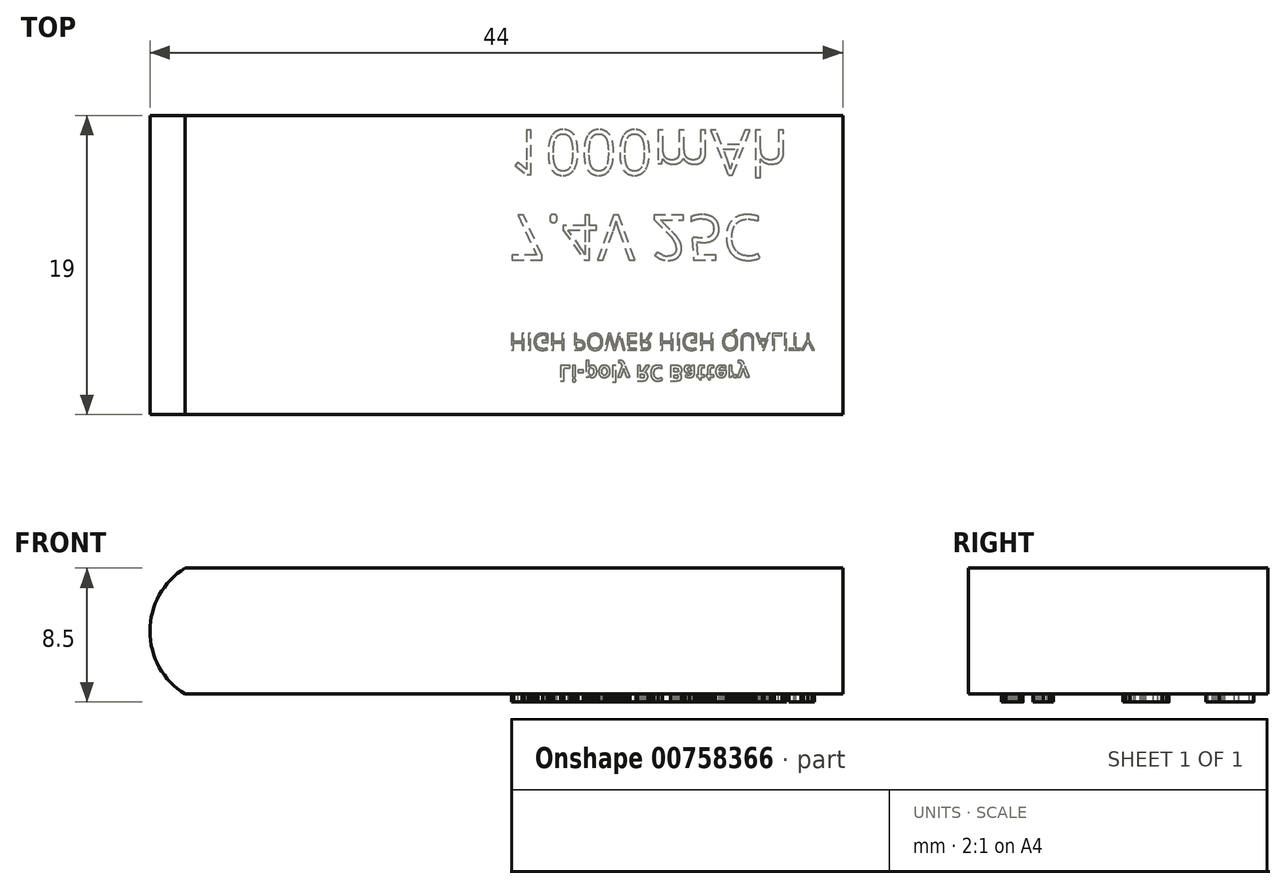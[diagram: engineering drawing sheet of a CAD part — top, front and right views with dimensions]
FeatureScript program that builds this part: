
annotation { "Feature Type Name" : "Feature", "Feature Type Description" : "" }
export const myFeature = defineFeature(function(context is Context, id is Id, definition is map)
    precondition{}
    {
        {
            var Q0;
            Q0=qCreatedBy(makeId("Front.planeOp"),FACE);
            var sketch = newSketch(context, id + "F0", { "sketchPlane" : qUnion([Q0])});
            skLineSegment(sketch, "E0.bottom", {"start": v(22, 4) * mm, "end": v(-22, 4) * mm});
            skLineSegment(sketch, "E0.top", {"start": v(22, -4) * mm, "end": v(-22, -4) * mm});
            skLineSegment(sketch, "E0.left", {"start": v(22, 4) * mm, "end": v(22, -4) * mm});
            skLineSegment(sketch, "E0.right", {"start": v(-22, 4) * mm, "end": v(-22, -4) * mm});
            skPoint(sketch, "E0.middle", {"position": v(0, 0) * mm});
            skArc(sketch, "E1", {"start": v(-22, 0) * mm, "mid": v(-21.4, -2.3) * mm, "end": v(-19.76, -4) * mm});
            skArc(sketch, "E2", {"start": v(-22, 0) * mm, "mid": v(-21.4, 2.3) * mm, "end": v(-19.76, 4) * mm});
            skSolve(sketch);
        }
        {
            var Q0;
            {var subQ1=sQuery(id+"F0.wireOp",EDGE,"E0.left");Q0=makeQuery(id+"F0.imprint","IMPRINT",FACE,{"disambiguationData":[TD([[makeQuery(id+"F0.imprint","IMPRINT",EDGE,{"derivedFrom":subQ1}),-1.0]])]});}
            extrude(context, id + "F1", {"entities" : qUnion([Q0]), "endBound" : BoundingType.SYMMETRIC, "depth" : 19 * mm});
        }
        {
            var Q0;
            Q0=makeQuery(id+"F1.opExtrude","SWEPT_FACE",FACE,{"disambiguationData":[OSD([sQuery(id+"F0.wireOp",EDGE,"E0.top")])]});
            var sketch = newSketch(context, id + "F2", { "sketchPlane" : qUnion([Q0])});
            skText(sketch, "E3", { "text": "Li-poly RC Battery", "fontName": "OpenSans-Bold.ttf"});
            skText(sketch, "E4", { "text": "HIGH POWER HIGH QUALITY", "fontName": "OpenSans-Regular.ttf"});
            skText(sketch, "E5", { "text": "7.4V 25C\n1000mAh", "fontName": "OpenSans-Regular.ttf"});
            const initialGuessF2  = {"E3": [0.00396, 0.00638, 1, 0, 0.00098], "E4": [0.00083, 0.00436, 1, 0, 0.00105], "E5": [0.00083, -0.00317, 1, 0, 0.00286]};
            skSetInitialGuess(sketch, initialGuessF2);
            skSolve(sketch);
        }
        {
            var Q0;
            Q0=qSketchRegion(id+"F2",true);
            extrude(context, id + "F3", {"entities" : qUnion([Q0]), "operationType" : NewBodyOperationType.ADD, "depth" : .5 * mm});
        }
    });
